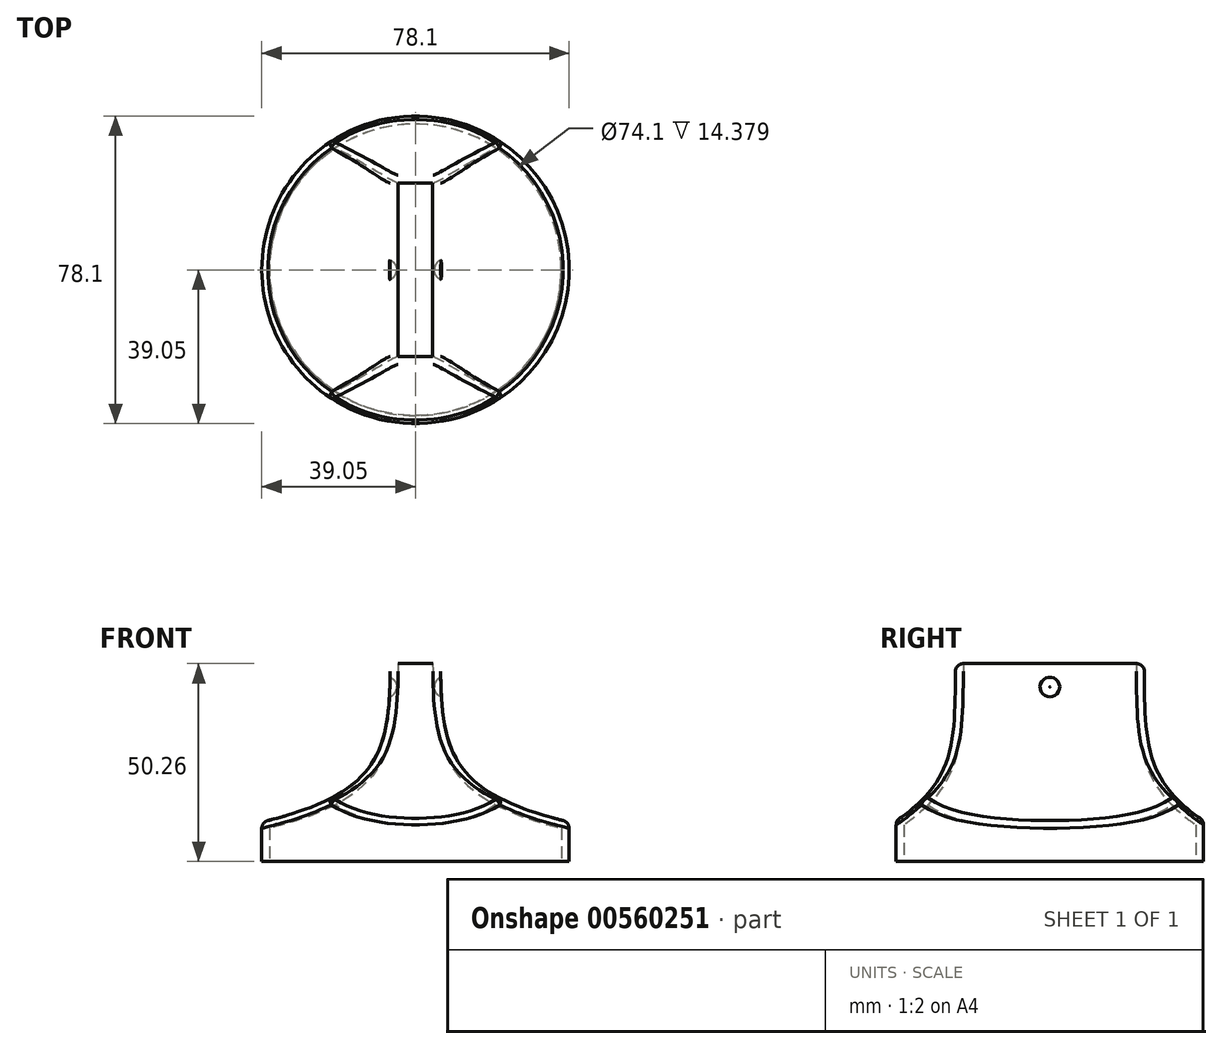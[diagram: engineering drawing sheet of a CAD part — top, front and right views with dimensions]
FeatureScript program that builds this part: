
annotation { "Feature Type Name" : "Feature", "Feature Type Description" : "" }
export const myFeature = defineFeature(function(context is Context, id is Id, definition is map)
    precondition{}
    {
        {
            var Q0;
            Q0=qCreatedBy(makeId("Top.planeOp"),FACE);
            var sketch = newSketch(context, id + "F0", { "sketchPlane" : qUnion([Q0])});
            skLineSegment(sketch, "E0.bottom", {"start": v(39.05, 39.05) * mm, "end": v(-39.05, 39.05) * mm});
            skLineSegment(sketch, "E0.top", {"start": v(39.05, -39.05) * mm, "end": v(-39.05, -39.05) * mm});
            skLineSegment(sketch, "E0.left", {"start": v(39.05, 39.05) * mm, "end": v(39.05, -39.05) * mm});
            skLineSegment(sketch, "E0.right", {"start": v(-39.05, 39.05) * mm, "end": v(-39.05, -39.05) * mm});
            skPoint(sketch, "E0.middle", {"position": v(0, 0) * mm});
            skSolve(sketch);
        }
        {
            var Q0;
            Q0 = qSketchRegion(id + "F0", true);
            extrude(context, id + "F1", {"entities" : qUnion([Q0]), "depth" : 50.8 * mm, "offsetDistance" : 25.4 * mm});
        }
        {
            var Q0;
            Q0=makeQuery(id+"F1.opExtrude","SWEPT_FACE",FACE,{"disambiguationData":[OSD([sQuery(id+"F0.wireOp",EDGE,"E0.bottom")])]});
            var sketch = newSketch(context, id + "F2", { "sketchPlane" : qUnion([Q0])});
            skFitSpline(sketch, "E1", {"points": [v(-6.4, 50.8) * mm, v(-11.41, 24.4) * mm, v(-39.05, 10) * mm], "startDerivative": vector(0.05, -69.07) * mm, "endDerivative": vector(-77.08, -18.22) * mm});
            skLineSegment(sketch, "E2", {"start": v(-6.4, 50.8) * mm, "end": v(-39.05, 50.8) * mm});
            skLineSegment(sketch, "E3", {"start": v(-39.05, 50.8) * mm, "end": v(-39.05, 10) * mm});
            skFitSpline(sketch, "E4.MirrorCS", {"points": [v(6.4, 50.8) * mm, v(11.41, 24.4) * mm, v(39.05, 10) * mm], "startDerivative": vector(-0.05, -69.07) * mm, "endDerivative": vector(77.08, -18.22) * mm});
            skLineSegment(sketch, "E5.MirrorCS", {"start": v(6.4, 50.8) * mm, "end": v(39.05, 50.8) * mm});
            skLineSegment(sketch, "E6.MirrorCS", {"start": v(39.05, 50.8) * mm, "end": v(39.05, 10) * mm});
            skSolve(sketch);
        }
        {
            var Q0;
            Q0 = qSketchRegion(id + "F2", true);
            extrude(context, id + "F3", {"entities" : qUnion([Q0]), "operationType" : NewBodyOperationType.REMOVE, "endBound" : BoundingType.THROUGH_ALL, "oppositeDirection" : true, "depth" : 25.4 * mm, "offsetDistance" : 25.4 * mm});
        }
        {
            var Q0;
            Q0=makeQuery(id+"F1.opExtrude","CAP_FACE",FACE,{"disambiguationData":[OSD([sQuery(id+"F0.wireOp",EDGE,"E0.bottom"),sQuery(id+"F0.wireOp",EDGE,"E0.top"),sQuery(id+"F0.wireOp",EDGE,"E0.left"),sQuery(id+"F0.wireOp",EDGE,"E0.right")])],"isStart":true});
            var sketch = newSketch(context, id + "F4", { "sketchPlane" : qUnion([Q0])});
            skCircle(sketch, "E7", {"center": v(0, 0) * mm, "radius": 39.05 * mm});
            skSolve(sketch);
        }
        {
            var Q0;
            {var subQ0=sQuery(id+"F4.wireOp",EDGE,"E7");var subQ1=makeQuery(id+"F1.opExtrude","CAP_EDGE",EDGE,{"disambiguationData":[OSD([sQuery(id+"F0.wireOp",EDGE,"E0.left")])],"isStart":true});var subQ2=makeQuery(id+"F4.imprint","INTERSECT",VERTEX,{"derivedFrom":[subQ1,subQ0]});Q0=makeQuery(id+"F4.imprint","IMPRINT",FACE,{"disambiguationData":[TD([[makeQuery(id+"F4.imprint","IMPRINT",EDGE,{"disambiguationData":[TD([[subQ2,1.0]])],"derivedFrom":subQ0}),-1.0]])]});}
            var Q1;
            {var subQ0=sQuery(id+"F4.wireOp",EDGE,"E7");var subQ1=makeQuery(id+"F1.opExtrude","CAP_EDGE",EDGE,{"disambiguationData":[OSD([sQuery(id+"F0.wireOp",EDGE,"E0.right")])],"isStart":true});var subQ2=makeQuery(id+"F4.imprint","INTERSECT",VERTEX,{"derivedFrom":[subQ1,subQ0]});Q1=makeQuery(id+"F4.imprint","IMPRINT",FACE,{"disambiguationData":[TD([[makeQuery(id+"F4.imprint","IMPRINT",EDGE,{"disambiguationData":[TD([[subQ2,-1.0]])],"derivedFrom":subQ0}),-1.0]])]});}
            var Q2;
            {var subQ0=sQuery(id+"F4.wireOp",EDGE,"E7");var subQ1=makeQuery(id+"F1.opExtrude","CAP_EDGE",EDGE,{"disambiguationData":[OSD([sQuery(id+"F0.wireOp",EDGE,"E0.top")])],"isStart":true});var subQ2=makeQuery(id+"F4.imprint","INTERSECT",VERTEX,{"derivedFrom":[subQ1,subQ0]});Q2=makeQuery(id+"F4.imprint","IMPRINT",FACE,{"disambiguationData":[TD([[makeQuery(id+"F4.imprint","IMPRINT",EDGE,{"disambiguationData":[TD([[subQ2,1.0]])],"derivedFrom":subQ0}),-1.0]])]});}
            var Q3;
            {var subQ0=sQuery(id+"F4.wireOp",EDGE,"E7");var subQ1=makeQuery(id+"F1.opExtrude","CAP_EDGE",EDGE,{"disambiguationData":[OSD([sQuery(id+"F0.wireOp",EDGE,"E0.top")])],"isStart":true});var subQ2=makeQuery(id+"F4.imprint","INTERSECT",VERTEX,{"derivedFrom":[subQ1,subQ0]});Q3=makeQuery(id+"F4.imprint","IMPRINT",FACE,{"disambiguationData":[TD([[makeQuery(id+"F4.imprint","IMPRINT",EDGE,{"disambiguationData":[TD([[subQ2,-1.0]])],"derivedFrom":subQ0}),-1.0]])]});}
            extrude(context, id + "F5", {"entities" : qUnion([Q0, Q1, Q2, Q3]), "operationType" : NewBodyOperationType.REMOVE, "endBound" : BoundingType.THROUGH_ALL, "oppositeDirection" : true, "depth" : 25.4 * mm, "offsetDistance" : 25.4 * mm});
        }
        {
            var Q0;
            Q0=qCreatedBy(makeId("Right.planeOp"),FACE);
            var sketch = newSketch(context, id + "F6", { "sketchPlane" : qUnion([Q0])});
            skLineSegment(sketch, "E8.top", {"start": v(24, 50.26) * mm, "end": v(-24, 50.26) * mm});
            skPoint(sketch, "E8.middle", {"position": v(0, 47.85) * mm});
            skPoint(sketch, "E8.bottom.end.orphan", {"position": v(-24, 45.43) * mm});
            skPoint(sketch, "E8.left.start.orphan", {"position": v(24, 45.43) * mm});
            skFitSpline(sketch, "E9", {"points": [v(-24, 50.26) * mm, v(-27.02, 23.49) * mm, v(-39.57, 10) * mm], "startDerivative": vector(-0.16, -57.64) * mm, "endDerivative": vector(-33.37, -21.46) * mm});
            skLineSegment(sketch, "E10", {"start": v(-40.45, 52.33) * mm, "end": v(-43.17, 14.06) * mm});
            skLineSegment(sketch, "E11", {"start": v(-43.17, 14.06) * mm, "end": v(-39.57, 10) * mm});
            skFitSpline(sketch, "E12.MirrorCS", {"points": [v(24, 50.26) * mm, v(27.02, 23.49) * mm, v(39.57, 10) * mm], "startDerivative": vector(0.16, -57.64) * mm, "endDerivative": vector(33.37, -21.46) * mm});
            skLineSegment(sketch, "E13.MirrorCS", {"start": v(40.45, 52.33) * mm, "end": v(43.17, 14.06) * mm});
            skLineSegment(sketch, "E14.MirrorCS", {"start": v(43.17, 14.06) * mm, "end": v(39.57, 10) * mm});
            skLineSegment(sketch, "E15", {"start": v(40.45, 52.33) * mm, "end": v(24, 52.33) * mm});
            skLineSegment(sketch, "E16", {"start": v(24, 52.33) * mm, "end": v(24, 50.26) * mm});
            skLineSegment(sketch, "E17", {"start": v(-24, 52.33) * mm, "end": v(-40.45, 52.33) * mm});
            skLineSegment(sketch, "E18", {"start": v(-24, 52.33) * mm, "end": v(-24, 50.26) * mm});
            skLineSegment(sketch, "E19", {"start": v(-24, 52.33) * mm, "end": v(24, 52.33) * mm});
            skSolve(sketch);
        }
        {
            var Q0;
            Q0 = qSketchRegion(id + "F6", true);
            extrude(context, id + "F7", {"entities" : qUnion([Q0]), "operationType" : NewBodyOperationType.REMOVE, "endBound" : BoundingType.THROUGH_ALL, "oppositeDirection" : true, "depth" : 25.4 * mm, "offsetDistance" : 25.4 * mm, "hasSecondDirection" : true, "secondDirectionBound" : SecondDirectionBoundingType.THROUGH_ALL, "secondDirectionOppositeDirection" : false, "secondDirectionDepth" : 25.4 * mm});
        }
        {
            var Q0;
            Q0=makeQuery(id+"F7.boolean.opBoolean","COPY",FACE,{"derivedFrom":makeQuery(id+"F7.opExtrude","SWEPT_FACE",FACE,{"disambiguationData":[OSD([sQuery(id+"F6.wireOp",EDGE,"E8.top")])]})});
            var Q1;
            Q1=makeQuery(id+"F1.opExtrude","CAP_FACE",FACE,{"disambiguationData":[OSD([sQuery(id+"F0.wireOp",EDGE,"E0.bottom"),sQuery(id+"F0.wireOp",EDGE,"E0.top"),sQuery(id+"F0.wireOp",EDGE,"E0.left"),sQuery(id+"F0.wireOp",EDGE,"E0.right")])],"isStart":true});
            shell(context, id + "F8", {"entities" : qUnion([Q0, Q1]), "thickness" : 2 * mm});
        }
        {
            var Q0;
            Q0=makeQuery(id+"F3.boolean.opBoolean","COPY",FACE,{"derivedFrom":makeQuery(id+"F3.opExtrude","SWEPT_FACE",FACE,{"disambiguationData":[OSD([sQuery(id+"F2.wireOp",EDGE,"E4.MirrorCS")])]})});
            var Q1;
            Q1=makeQuery(id+"F7.boolean.opBoolean","COPY",FACE,{"derivedFrom":makeQuery(id+"F7.opExtrude","SWEPT_FACE",FACE,{"disambiguationData":[OSD([sQuery(id+"F6.wireOp",EDGE,"E9")])]})});
            var Q2;
            Q2=makeQuery(id+"F3.boolean.opBoolean","COPY",FACE,{"derivedFrom":makeQuery(id+"F3.opExtrude","SWEPT_FACE",FACE,{"disambiguationData":[OSD([sQuery(id+"F2.wireOp",EDGE,"E1")])]})});
            var Q3;
            Q3=makeQuery(id+"F7.boolean.opBoolean","COPY",FACE,{"derivedFrom":makeQuery(id+"F7.opExtrude","SWEPT_FACE",FACE,{"disambiguationData":[OSD([sQuery(id+"F6.wireOp",EDGE,"E12.MirrorCS")])]})});
            fillet(context, id + "F9", {"entities" : qUnion([Q0, Q1, Q2, Q3]), "radius" : 2 * mm, "tangentPropagation" : true, "allowEdgeOverflow" : false});
        }
        {
            var Q0;
            Q0=qCreatedBy(makeId("Right.planeOp"),FACE);
            cPlane(context, id + "F10", {"entities" : qUnion([Q0]), "cplaneType" : CPlaneType.OFFSET, "offset" : 6.4 * mm, "width" : 152.4 * mm, "height" : 152.4 * mm});
        }
        {
            var Q0;
            Q0=qCreatedBy(id+"F10.planeOp",FACE);
            var sketch = newSketch(context, id + "F11", { "sketchPlane" : qUnion([Q0])});
            skCircle(sketch, "E20", {"center": v(0, 44.28) * mm, "radius": 2.5 * mm});
            skSolve(sketch);
        }
        {
            var Q0;
            Q0 = qSketchRegion(id + "F11", true);
            extrude(context, id + "F12", {"entities" : qUnion([Q0]), "operationType" : NewBodyOperationType.REMOVE, "oppositeDirection" : true, "depth" : 1.6 * mm, "offsetDistance" : 25.4 * mm, "hasSecondDirection" : true, "secondDirectionBound" : SecondDirectionBoundingType.THROUGH_ALL, "secondDirectionOppositeDirection" : false, "secondDirectionDepth" : 25.4 * mm});
        }
        {
            var Q0;
            Q0=qCreatedBy(makeId("Right.planeOp"),FACE);
            cPlane(context, id + "F13", {"entities" : qUnion([Q0]), "cplaneType" : CPlaneType.OFFSET, "offset" : 6.4 * mm, "oppositeDirection" : true, "width" : 152.4 * mm, "height" : 152.4 * mm});
        }
        {
            var Q0;
            Q0=qCreatedBy(id+"F13.planeOp",FACE);
            var sketch = newSketch(context, id + "F14", { "sketchPlane" : qUnion([Q0])});
            skCircle(sketch, "E21", {"center": v(0, 44.28) * mm, "radius": 2.5 * mm});
            skSolve(sketch);
        }
        {
            var Q0;
            Q0 = qSketchRegion(id + "F14", true);
            extrude(context, id + "F15", {"entities" : qUnion([Q0]), "operationType" : NewBodyOperationType.REMOVE, "depth" : 1.6 * mm, "offsetDistance" : 25.4 * mm, "hasSecondDirection" : true, "secondDirectionBound" : SecondDirectionBoundingType.THROUGH_ALL, "secondDirectionOppositeDirection" : true, "secondDirectionDepth" : 25.4 * mm});
        }
        {
            var Q0;
            Q0=makeQuery(id+"F12.boolean.opBoolean","COPY",EDGE,{"derivedFrom":makeQuery(id+"F12.opExtrude","CAP_EDGE",EDGE,{"disambiguationData":[OSD([sQuery(id+"F11.wireOp",EDGE,"E20")])],"isStart":false})});
            var Q1;
            Q1=makeQuery(id+"F15.boolean.opBoolean","COPY",FACE,{"derivedFrom":makeQuery(id+"F15.opExtrude","CAP_FACE",FACE,{"disambiguationData":[OSD([sQuery(id+"F14.wireOp",EDGE,"E21")])],"isStart":false})});
            fillet(context, id + "F16", {"entities" : qUnion([Q0, Q1]), "radius" : 2.6 * mm, "tangentPropagation" : true, "allowEdgeOverflow" : false});
        }
    });
